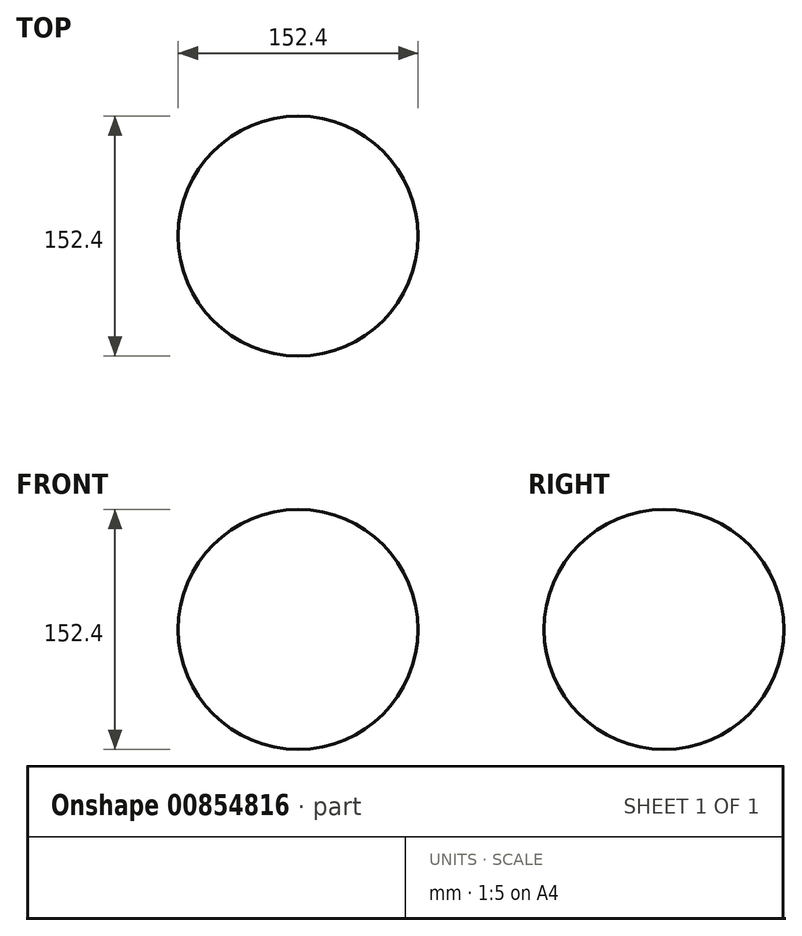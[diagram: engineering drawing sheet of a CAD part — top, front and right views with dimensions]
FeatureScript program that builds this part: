
annotation { "Feature Type Name" : "Feature", "Feature Type Description" : "" }
export const myFeature = defineFeature(function(context is Context, id is Id, definition is map)
    precondition{}
    {
        {
            var Q0;
            Q0=qCreatedBy(makeId("Top.planeOp"),FACE);
            var sketch = newSketch(context, id + "F0", { "sketchPlane" : qUnion([Q0])});
            skCircle(sketch, "E0", {"center": v(0, 0) * mm, "radius": 76.2 * mm});
            skSolve(sketch);
        }
        {
            var Q0;
            Q0=makeQuery(id+"F0.imprint","IMPRINT",FACE,{"disambiguationData":[TD([[makeQuery(id+"F0.imprint","IMPRINT",EDGE,{"derivedFrom":sQuery(id+"F0.wireOp",EDGE,"E0")}),1.0]])]});
            extrude(context, id + "F1", {"entities" : qUnion([Q0]), "depth" : 76.2 * mm, "offsetDistance" : 25.4 * mm});
        }
        {
            var Q0;
            Q0=makeQuery(id+"F1.opExtrude","CAP_FACE",FACE,{"disambiguationData":[OSD([sQuery(id+"F0.wireOp",EDGE,"E0")])],"isStart":true});
            extrude(context, id + "F2", {"entities" : qUnion([Q0]), "operationType" : NewBodyOperationType.ADD, "depth" : 76.2 * mm, "offsetDistance" : 25.4 * mm});
        }
        {
            var Q0;
            Q0=makeQuery(id+"F2.opExtrude","CAP_EDGE",EDGE,{"disambiguationData":[OSD([sQuery(id+"F0.wireOp",EDGE,"E0")])],"isStart":false});
            var Q1;
            Q1=makeQuery(id+"F1.opExtrude","CAP_EDGE",EDGE,{"disambiguationData":[OSD([sQuery(id+"F0.wireOp",EDGE,"E0")])],"isStart":false});
            fillet(context, id + "F3", {"entities" : qUnion([Q0, Q1]), "radius" : 76.2 * mm, "tangentPropagation" : true, "allowEdgeOverflow" : false});
        }
    });
